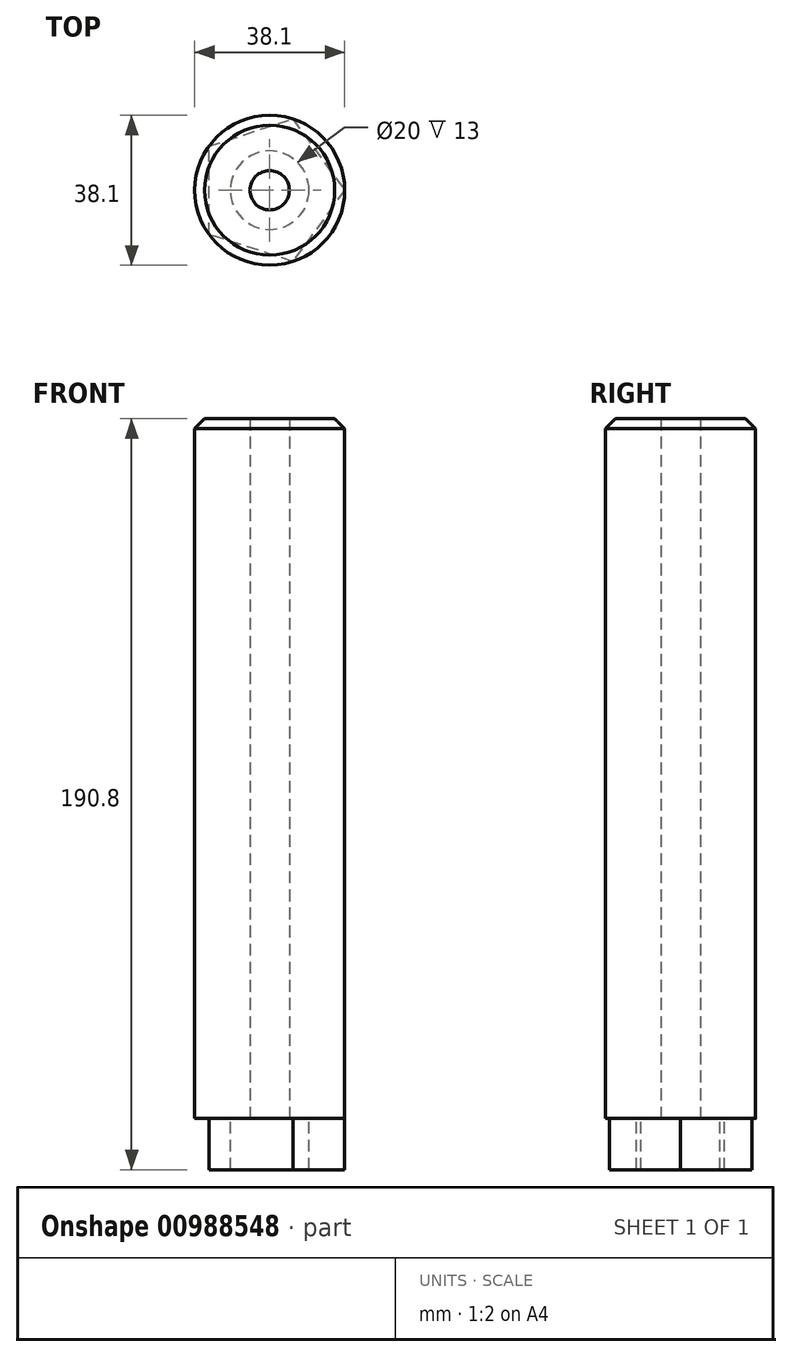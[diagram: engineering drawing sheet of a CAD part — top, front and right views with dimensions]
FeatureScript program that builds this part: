
annotation { "Feature Type Name" : "Feature", "Feature Type Description" : "" }
export const myFeature = defineFeature(function(context is Context, id is Id, definition is map)
    precondition{}
    {
        {
            var Q0;
            Q0=qCreatedBy(makeId("Top.planeOp"),FACE);
            var sketch = newSketch(context, id + "F0", { "sketchPlane" : qUnion([Q0])});
            skCircle(sketch, "E0", {"center": v(0, 0) * mm, "radius": 19.05 * mm});
            skCircle(sketch, "E1", {"center": v(0, 0) * mm, "radius": 5 * mm});
            skSolve(sketch);
        }
        {
            var Q0;
            Q0=makeQuery(id+"F0.imprint","IMPRINT",FACE,{"disambiguationData":[TD([[makeQuery(id+"F0.imprint","IMPRINT",EDGE,{"derivedFrom":sQuery(id+"F0.wireOp",EDGE,"E0")}),1.0]])]});
            extrude(context, id + "F1", {"entities" : qUnion([Q0]), "depth" : 177.8 * mm, "offsetDistance" : 25.4 * mm});
        }
        {
            var Q0;
            Q0=qCreatedBy(makeId("Top.planeOp"),FACE);
            var sketch = newSketch(context, id + "F2", { "sketchPlane" : qUnion([Q0])});
            skCircle(sketch, "E2.cCircle", {"center": v(0, 0) * mm, "radius": 19.05 * mm, "construction": true});
            skLineSegment(sketch, "E2.0", {"start": v(19.05, 0) * mm, "end": v(5.89, -18.12) * mm});
            skLineSegment(sketch, "E2.1", {"start": v(5.89, -18.12) * mm, "end": v(-15.41, -11.2) * mm});
            skLineSegment(sketch, "E2.2", {"start": v(-15.41, -11.2) * mm, "end": v(-15.41, 11.2) * mm});
            skLineSegment(sketch, "E2.3", {"start": v(-15.41, 11.2) * mm, "end": v(5.89, 18.12) * mm});
            skLineSegment(sketch, "E2.4", {"start": v(5.89, 18.12) * mm, "end": v(19.05, 0) * mm});
            skCircle(sketch, "E3", {"center": v(0, 0) * mm, "radius": 10 * mm});
            skSolve(sketch);
        }
        {
            var Q0;
            Q0=makeQuery(id+"F2.imprint","IMPRINT",FACE,{"disambiguationData":[TD([[makeQuery(id+"F2.imprint","IMPRINT",EDGE,{"derivedFrom":sQuery(id+"F2.wireOp",EDGE,"E2.0")}),-1.0]])]});
            extrude(context, id + "F3", {"entities" : qUnion([Q0]), "operationType" : NewBodyOperationType.ADD, "depth" : -13 * mm, "offsetDistance" : 25.4 * mm});
        }
        {
            var Q0;
            Q0=makeQuery(id+"F1.opExtrude","CAP_EDGE",EDGE,{"disambiguationData":[OSD([sQuery(id+"F0.wireOp",EDGE,"E0")])],"isStart":false});
            chamfer(context, id + "F4", {"entities" : qUnion([Q0]), "width" : 2.54 * mm, "tangentPropagation" : true});
        }
    });
